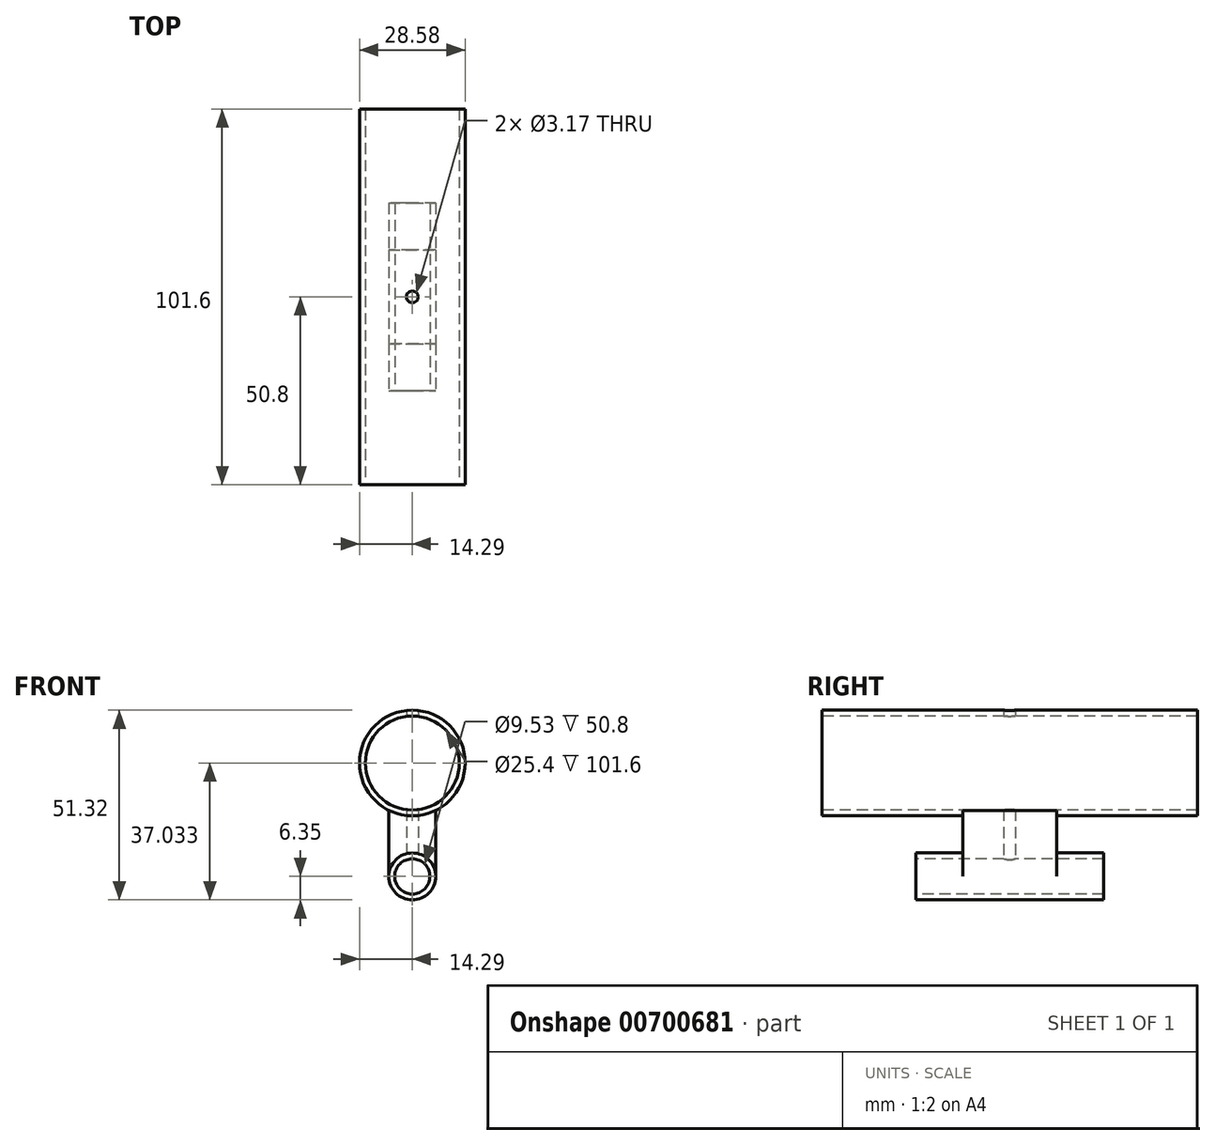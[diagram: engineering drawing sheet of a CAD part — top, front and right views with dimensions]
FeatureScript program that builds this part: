
annotation { "Feature Type Name" : "Feature", "Feature Type Description" : "" }
export const myFeature = defineFeature(function(context is Context, id is Id, definition is map)
    precondition{}
    {
        {
            var Q0;
            Q0=qCreatedBy(makeId("Front.planeOp"),FACE);
            var sketch = newSketch(context, id + "F0", { "sketchPlane" : qUnion([Q0])});
            skCircle(sketch, "E0", {"center": v(0, 0) * mm, "radius": 4.76 * mm});
            skArc(sketch, "E1", {"start": v(-6.35, 0) * mm, "mid": v(0, -6.35) * mm, "end": v(6.35, 0) * mm});
            skPoint(sketch, "E2", {"position": v(0, 30.68) * mm});
            skCircle(sketch, "E3", {"center": v(0, 30.68) * mm, "radius": 12.7 * mm});
            skCircle(sketch, "E4", {"center": v(0, 30.68) * mm, "radius": 14.29 * mm});
            skLineSegment(sketch, "E5", {"start": v(-6.35, 0) * mm, "end": v(-6.35, 17.88) * mm});
            skLineSegment(sketch, "E6", {"start": v(6.35, 0) * mm, "end": v(6.35, 17.88) * mm});
            skSolve(sketch);
        }
        {
            var Q0;
            Q0 = qSketchRegion(id + "F0", true);
            extrude(context, id + "F1", {"entities" : qUnion([Q0]), "oppositeDirection" : true, "depth" : 101.6 * mm, "offsetDistance" : 25.4 * mm});
        }
        {
            var Q0;
            Q0=makeQuery(id+"F1.opExtrude","CAP_FACE",FACE,{"disambiguationData":[OSD([sQuery(id+"F0.wireOp",EDGE,"E0"),sQuery(id+"F0.wireOp",EDGE,"E1"),sQuery(id+"F0.wireOp",EDGE,"E3"),sQuery(id+"F0.wireOp",EDGE,"E4"),sQuery(id+"F0.wireOp",EDGE,"E5"),sQuery(id+"F0.wireOp",EDGE,"E6")])],"isStart":true});
            var sketch = newSketch(context, id + "F2", { "sketchPlane" : qUnion([Q0])});
            skArc(sketch, "E7", {"start": v(-6.35, 17.88) * mm, "mid": v(0, 16.4) * mm, "end": v(6.35, 17.88) * mm});
            skArc(sketch, "E8.0", {"start": v(-6.35, 0) * mm, "mid": v(0, -6.35) * mm, "end": v(6.35, 0) * mm});
            skLineSegment(sketch, "E9", {"start": v(-6.35, 17.88) * mm, "end": v(-6.35, 0) * mm});
            skLineSegment(sketch, "E10", {"start": v(6.35, 17.88) * mm, "end": v(6.35, 0) * mm});
            skSolve(sketch);
        }
        {
            var Q0;
            Q0 = qSketchRegion(id + "F2", true);
            extrude(context, id + "F3", {"entities" : qUnion([Q0]), "operationType" : NewBodyOperationType.REMOVE, "oppositeDirection" : true, "depth" : 25.4 * mm, "offsetDistance" : 25.4 * mm});
        }
        {
            var Q0;
            Q0=makeQuery(id+"F1.opExtrude","CAP_FACE",FACE,{"disambiguationData":[OSD([sQuery(id+"F0.wireOp",EDGE,"E0"),sQuery(id+"F0.wireOp",EDGE,"E1"),sQuery(id+"F0.wireOp",EDGE,"E3"),sQuery(id+"F0.wireOp",EDGE,"E4"),sQuery(id+"F0.wireOp",EDGE,"E5"),sQuery(id+"F0.wireOp",EDGE,"E6")])],"isStart":false});
            var sketch = newSketch(context, id + "F4", { "sketchPlane" : qUnion([Q0])});
            skArc(sketch, "E11", {"start": v(-6.35, 17.88) * mm, "mid": v(0, 16.4) * mm, "end": v(6.35, 17.88) * mm});
            skArc(sketch, "E12.0", {"start": v(6.35, 0) * mm, "mid": v(0, -6.35) * mm, "end": v(-6.35, 0) * mm});
            skLineSegment(sketch, "E13", {"start": v(-6.35, 0) * mm, "end": v(-6.35, 17.88) * mm});
            skLineSegment(sketch, "E14", {"start": v(6.35, 17.88) * mm, "end": v(6.35, 0) * mm});
            skSolve(sketch);
        }
        {
            var Q0;
            Q0 = qSketchRegion(id + "F4", true);
            extrude(context, id + "F5", {"entities" : qUnion([Q0]), "operationType" : NewBodyOperationType.REMOVE, "oppositeDirection" : true, "depth" : 25.4 * mm, "offsetDistance" : 25.4 * mm});
        }
        {
            var Q0;
            Q0=makeQuery(id+"F5.boolean.opBoolean","COPY",FACE,{"derivedFrom":makeQuery(id+"F5.opExtrude","CAP_FACE",FACE,{"disambiguationData":[OSD([sQuery(id+"F4.wireOp",EDGE,"E11"),sQuery(id+"F4.wireOp",EDGE,"E12.0"),sQuery(id+"F4.wireOp",EDGE,"E13"),sQuery(id+"F4.wireOp",EDGE,"E14")])],"isStart":false})});
            var sketch = newSketch(context, id + "F6", { "sketchPlane" : qUnion([Q0])});
            skArc(sketch, "E15", {"start": v(6.35, 0) * mm, "mid": v(0, 6.35) * mm, "end": v(-6.35, 0) * mm});
            skLineSegment(sketch, "E16", {"start": v(-6.35, 0) * mm, "end": v(-6.35, 17.88) * mm});
            skLineSegment(sketch, "E17", {"start": v(6.35, 0) * mm, "end": v(6.35, 17.88) * mm});
            skArc(sketch, "E18.0", {"start": v(-6.35, 17.88) * mm, "mid": v(0, 16.4) * mm, "end": v(6.35, 17.88) * mm});
            skSolve(sketch);
        }
        {
            var Q0;
            Q0 = qSketchRegion(id + "F6", true);
            extrude(context, id + "F7", {"entities" : qUnion([Q0]), "operationType" : NewBodyOperationType.REMOVE, "oppositeDirection" : true, "depth" : 12.7 * mm, "offsetDistance" : 25.4 * mm});
        }
        {
            var Q0;
            Q0=makeQuery(id+"F3.boolean.opBoolean","COPY",FACE,{"derivedFrom":makeQuery(id+"F3.opExtrude","CAP_FACE",FACE,{"disambiguationData":[OSD([sQuery(id+"F2.wireOp",EDGE,"E7"),sQuery(id+"F2.wireOp",EDGE,"E8.0"),sQuery(id+"F2.wireOp",EDGE,"E9"),sQuery(id+"F2.wireOp",EDGE,"E10")])],"isStart":false})});
            var sketch = newSketch(context, id + "F8", { "sketchPlane" : qUnion([Q0])});
            skArc(sketch, "E19", {"start": v(6.35, 0) * mm, "mid": v(0, 6.35) * mm, "end": v(-6.35, 0) * mm});
            skArc(sketch, "E20.0.0", {"start": v(6.35, 17.88) * mm, "mid": v(0, 16.4) * mm, "end": v(-6.35, 17.88) * mm});
            skLineSegment(sketch, "E20.0.1", {"start": v(-6.35, 17.88) * mm, "end": v(-6.35, 0) * mm});
            skLineSegment(sketch, "E20.0.3", {"start": v(6.35, 0) * mm, "end": v(6.35, 17.88) * mm});
            skSolve(sketch);
        }
        {
            var Q0;
            Q0 = qSketchRegion(id + "F8", true);
            extrude(context, id + "F9", {"entities" : qUnion([Q0]), "operationType" : NewBodyOperationType.REMOVE, "oppositeDirection" : true, "depth" : 12.7 * mm, "offsetDistance" : 25.4 * mm});
        }
        {
            var Q0;
            Q0=qCreatedBy(makeId("Top.planeOp"),FACE);
            var sketch = newSketch(context, id + "F10", { "sketchPlane" : qUnion([Q0])});
            skPoint(sketch, "E21", {"position": v(0, 50.8) * mm});
            skCircle(sketch, "E22", {"center": v(0, 50.8) * mm, "radius": 1.59 * mm});
            skSolve(sketch);
        }
        {
            var Q0;
            Q0 = qSketchRegion(id + "F10", true);
            extrude(context, id + "F11", {"entities" : qUnion([Q0]), "operationType" : NewBodyOperationType.REMOVE, "depth" : 127 * mm, "offsetDistance" : 25.4 * mm});
        }
    });
